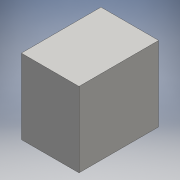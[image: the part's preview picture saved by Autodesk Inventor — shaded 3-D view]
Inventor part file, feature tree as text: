
AUTODESK INVENTOR PART (.ipt)
format: ipt  version: 2016 (Build 200138000, 138)  size: 151,040 bytes
history: native  units: mm
features: extrude x6, sketch x6
ambient origin geometry x8: Origin, YZ Plane, XZ Plane, XY Plane, X Axis, Y Axis, Z Axis, Center Point
bodies: Body1 (feature_tree)
feature tree (12):
  extrude  "Extrusion2"  Depth=548.0mm
  extrude  "Extrusion3"  Depth=583.0mm TaperAngle=0.0deg
  extrude  "Extrusion4"  Depth=345.0mm
  extrude  "Extrusion5"  Depth=88.0mm
  extrude  "Extrusion6"  Depth=75.0mm
  extrude  "Extrusion7"  Depth=583.0mm TaperAngle=0.0deg
  sketch  "Sketch1"  dims[d0=422.0mm d1=548.0mm]
  sketch  "Sketch2"  dims[d4=23.0mm d5=583.0mm d6=0.0mm]
  sketch  "Sketch3"  dims[d7=210.0mm d8=345.0mm]
  sketch  "Sketch4"  dims[d9=88.0mm d11=88.0mm]
  sketch  "Sketch5"  dims[d12=583.0mm d13=0.0mm d14=75.0mm]
  sketch  "Sketch6"  dims[d15=104.0mm d16=583.0mm d17=0.0mm d18=54.0mm d19=583.0mm d20=0.0mm d21=16.0mm d22=16.0mm d23=170.0mm d24=200.0mm d25=45.0mm d26=45.0mm d27=170.0mm d28=200.0mm d29=16.0mm d30=16.0mm d31=45.0mm d32=45.0mm d33=16.0mm d34=0.0mm d35=123.0mm d36=0.0mm]
